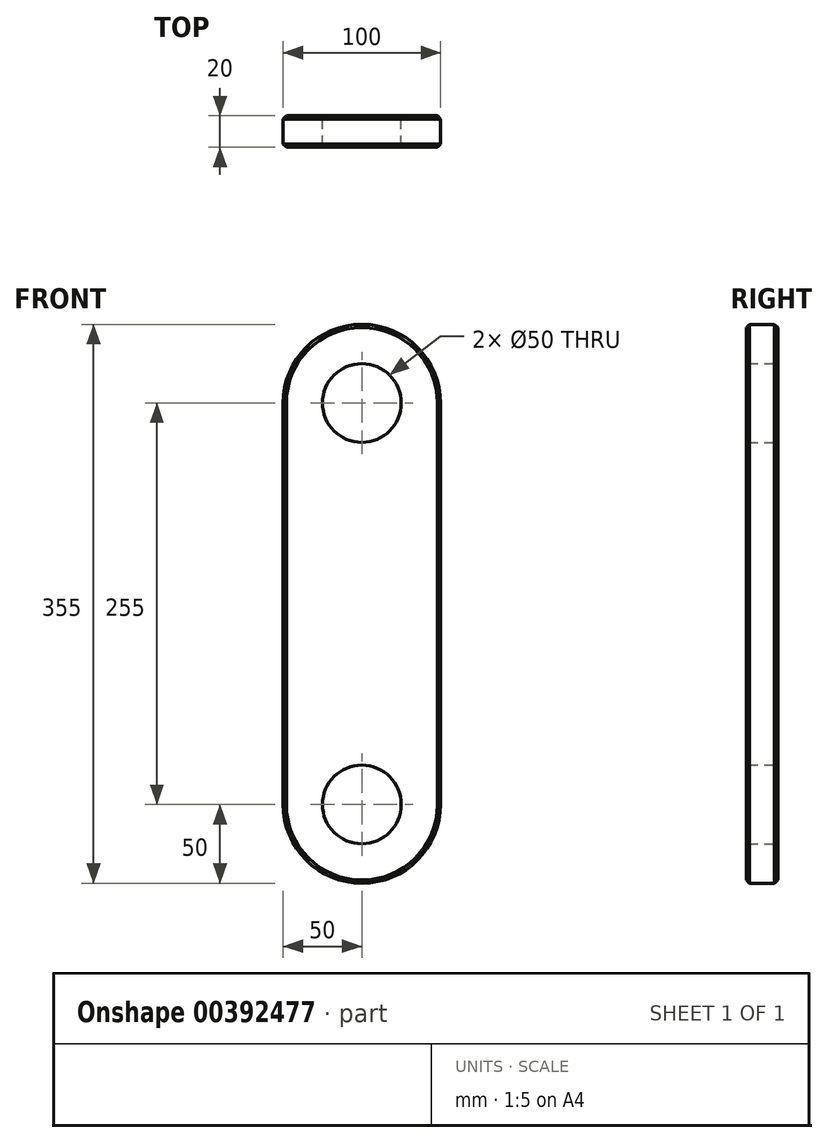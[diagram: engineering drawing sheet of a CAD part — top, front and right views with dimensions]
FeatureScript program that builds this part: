
annotation { "Feature Type Name" : "Feature", "Feature Type Description" : "" }
export const myFeature = defineFeature(function(context is Context, id is Id, definition is map)
    precondition{}
    {
        {
            var Q0;
            Q0=qCreatedBy(makeId("Front.planeOp"),FACE);
            var sketch = newSketch(context, id + "F0", { "sketchPlane" : qUnion([Q0])});
            skLineSegment(sketch, "E0.bottom", {"start": v(0, 0) * mm, "end": v(100, 0) * mm});
            skLineSegment(sketch, "E0.top", {"start": v(0, 255) * mm, "end": v(100, 255) * mm});
            skLineSegment(sketch, "E0.left", {"start": v(0, 0) * mm, "end": v(0, 255) * mm});
            skLineSegment(sketch, "E0.right", {"start": v(100, 0) * mm, "end": v(100, 255) * mm});
            skCircle(sketch, "E1", {"center": v(50, 255) * mm, "radius": 25 * mm});
            skCircle(sketch, "E2", {"center": v(50, 255) * mm, "radius": 50 * mm});
            skCircle(sketch, "E3", {"center": v(50, 0) * mm, "radius": 25 * mm});
            skCircle(sketch, "E4", {"center": v(50, 0) * mm, "radius": 50 * mm});
            skSolve(sketch);
        }
        {
            var Q0;
            Q0 = qSketchRegion(id + "F0", true);
            extrude(context, id + "F1", {"entities" : qUnion([Q0]), "depth" : 20 * mm});
        }
        {
            var Q0;
            Q0=makeQuery(id+"F1.opExtrude","CAP_EDGE",EDGE,{"disambiguationData":[OSD([sQuery(id+"F0.wireOp",EDGE,"E0.right")])],"isStart":false});
            var Q1;
            Q1=makeQuery(id+"F1.opExtrude","CAP_EDGE",EDGE,{"disambiguationData":[OSD([sQuery(id+"F0.wireOp",EDGE,"E0.right")])],"isStart":true});
            chamfer(context, id + "F2", {"entities" : qUnion([Q0, Q1]), "chamferType" : ChamferType.OFFSET_ANGLE, "width" : 2 * mm, "oppositeDirection" : false, "angle" : 45 * degree, "tangentPropagation" : true});
        }
    });
